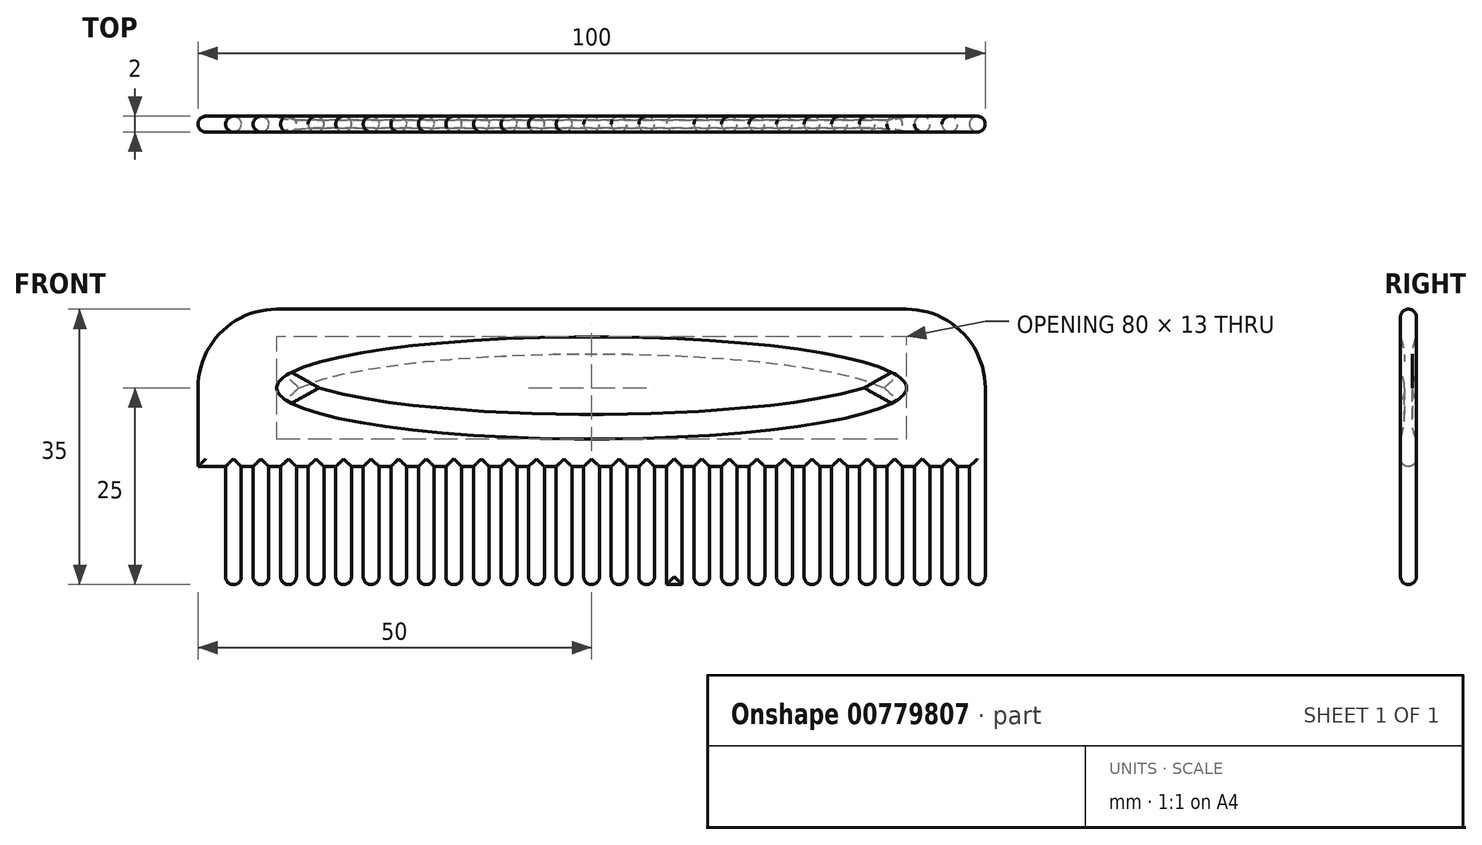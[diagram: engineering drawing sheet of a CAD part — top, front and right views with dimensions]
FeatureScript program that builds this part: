
annotation { "Feature Type Name" : "Feature", "Feature Type Description" : "" }
export const myFeature = defineFeature(function(context is Context, id is Id, definition is map)
    precondition{}
    {
        {
            var Q0;
            Q0=qCreatedBy(makeId("Front.planeOp"),FACE);
            var sketch = newSketch(context, id + "F0", { "sketchPlane" : qUnion([Q0])});
            skLineSegment(sketch, "E0.bottom", {"start": v(40, 10) * mm, "end": v(-40, 10) * mm});
            skLineSegment(sketch, "E0.top", {"start": v(50, -10) * mm, "end": v(-50, -10) * mm});
            skLineSegment(sketch, "E0.left", {"start": v(50, 0) * mm, "end": v(50, -10) * mm});
            skLineSegment(sketch, "E0.right", {"start": v(-50, 0) * mm, "end": v(-50, -10) * mm});
            skPoint(sketch, "E0.middle", {"position": v(0, 0) * mm});
            skPoint(sketch, "E1.visualSharp", {"position": v(-50, 10) * mm});
            skArc(sketch, "E1.filletArc", {"start": v(-40, 10) * mm, "mid": v(-47.07, 7.07) * mm, "end": v(-50, 0) * mm});
            skPoint(sketch, "E2.visualSharp", {"position": v(50, 10) * mm});
            skArc(sketch, "E2.filletArc", {"start": v(50, 0) * mm, "mid": v(47.07, 7.07) * mm, "end": v(40, 10) * mm});
            skLineSegment(sketch, "E3.bottom", {"start": v(-50, -10) * mm, "end": v(-48, -10) * mm});
            skLineSegment(sketch, "E3.top", {"start": v(-50, -25) * mm, "end": v(-48, -25) * mm});
            skLineSegment(sketch, "E3.left", {"start": v(-50, -10) * mm, "end": v(-50, -25) * mm});
            skLineSegment(sketch, "E3.right", {"start": v(-48, -10) * mm, "end": v(-48, -25) * mm});
            skLineSegment(sketch, "E4.1.0.0", {"start": v(-46.5, -10) * mm, "end": v(-46.5, -25) * mm});
            skLineSegment(sketch, "E4.1.0.1", {"start": v(-44.5, -10) * mm, "end": v(-44.5, -25) * mm});
            skLineSegment(sketch, "E4.1.0.2", {"start": v(-46.5, -25) * mm, "end": v(-44.5, -25) * mm});
            skLineSegment(sketch, "E4.2.0.0", {"start": v(-43, -10) * mm, "end": v(-43, -25) * mm});
            skLineSegment(sketch, "E4.2.0.1", {"start": v(-41, -10) * mm, "end": v(-41, -25) * mm});
            skLineSegment(sketch, "E4.2.0.2", {"start": v(-43, -25) * mm, "end": v(-41, -25) * mm});
            skLineSegment(sketch, "E4.3.0.0", {"start": v(-39.5, -10) * mm, "end": v(-39.5, -25) * mm});
            skLineSegment(sketch, "E4.3.0.1", {"start": v(-37.5, -10) * mm, "end": v(-37.5, -25) * mm});
            skLineSegment(sketch, "E4.3.0.2", {"start": v(-39.5, -25) * mm, "end": v(-37.5, -25) * mm});
            skLineSegment(sketch, "E4.4.0.0", {"start": v(-36, -10) * mm, "end": v(-36, -25) * mm});
            skLineSegment(sketch, "E4.4.0.1", {"start": v(-34, -10) * mm, "end": v(-34, -25) * mm});
            skLineSegment(sketch, "E4.4.0.2", {"start": v(-36, -25) * mm, "end": v(-34, -25) * mm});
            skLineSegment(sketch, "E4.5.0.0", {"start": v(-32.5, -10) * mm, "end": v(-32.5, -25) * mm});
            skLineSegment(sketch, "E4.5.0.1", {"start": v(-30.5, -10) * mm, "end": v(-30.5, -25) * mm});
            skLineSegment(sketch, "E4.5.0.2", {"start": v(-32.5, -25) * mm, "end": v(-30.5, -25) * mm});
            skLineSegment(sketch, "E4.6.0.0", {"start": v(-29, -10) * mm, "end": v(-29, -25) * mm});
            skLineSegment(sketch, "E4.6.0.1", {"start": v(-27, -10) * mm, "end": v(-27, -25) * mm});
            skLineSegment(sketch, "E4.6.0.2", {"start": v(-29, -25) * mm, "end": v(-27, -25) * mm});
            skLineSegment(sketch, "E4.7.0.0", {"start": v(-25.5, -10) * mm, "end": v(-25.5, -25) * mm});
            skLineSegment(sketch, "E4.7.0.1", {"start": v(-23.5, -10) * mm, "end": v(-23.5, -25) * mm});
            skLineSegment(sketch, "E4.7.0.2", {"start": v(-25.5, -25) * mm, "end": v(-23.5, -25) * mm});
            skLineSegment(sketch, "E4.8.0.0", {"start": v(-22, -10) * mm, "end": v(-22, -25) * mm});
            skLineSegment(sketch, "E4.8.0.1", {"start": v(-20, -10) * mm, "end": v(-20, -25) * mm});
            skLineSegment(sketch, "E4.8.0.2", {"start": v(-22, -25) * mm, "end": v(-20, -25) * mm});
            skLineSegment(sketch, "E4.9.0.0", {"start": v(-18.5, -10) * mm, "end": v(-18.5, -25) * mm});
            skLineSegment(sketch, "E4.9.0.1", {"start": v(-16.5, -10) * mm, "end": v(-16.5, -25) * mm});
            skLineSegment(sketch, "E4.9.0.2", {"start": v(-18.5, -25) * mm, "end": v(-16.5, -25) * mm});
            skLineSegment(sketch, "E4.10.0.0", {"start": v(-15, -10) * mm, "end": v(-15, -25) * mm});
            skLineSegment(sketch, "E4.10.0.1", {"start": v(-13, -10) * mm, "end": v(-13, -25) * mm});
            skLineSegment(sketch, "E4.10.0.2", {"start": v(-15, -25) * mm, "end": v(-13, -25) * mm});
            skLineSegment(sketch, "E4.11.0.0", {"start": v(-11.5, -10) * mm, "end": v(-11.5, -25) * mm});
            skLineSegment(sketch, "E4.11.0.1", {"start": v(-9.5, -10) * mm, "end": v(-9.5, -25) * mm});
            skLineSegment(sketch, "E4.11.0.2", {"start": v(-11.5, -25) * mm, "end": v(-9.5, -25) * mm});
            skLineSegment(sketch, "E4.12.0.0", {"start": v(-8, -10) * mm, "end": v(-8, -25) * mm});
            skLineSegment(sketch, "E4.12.0.1", {"start": v(-6, -10) * mm, "end": v(-6, -25) * mm});
            skLineSegment(sketch, "E4.12.0.2", {"start": v(-8, -25) * mm, "end": v(-6, -25) * mm});
            skLineSegment(sketch, "E4.13.0.0", {"start": v(-4.5, -10) * mm, "end": v(-4.5, -25) * mm});
            skLineSegment(sketch, "E4.13.0.1", {"start": v(-2.5, -10) * mm, "end": v(-2.5, -25) * mm});
            skLineSegment(sketch, "E4.13.0.2", {"start": v(-4.5, -25) * mm, "end": v(-2.5, -25) * mm});
            skLineSegment(sketch, "E4.14.0.0", {"start": v(-1, -10) * mm, "end": v(-1, -25) * mm});
            skLineSegment(sketch, "E4.14.0.1", {"start": v(1, -10) * mm, "end": v(1, -25) * mm});
            skLineSegment(sketch, "E4.14.0.2", {"start": v(-1, -25) * mm, "end": v(1, -25) * mm});
            skLineSegment(sketch, "E4.15.0.0", {"start": v(2.5, -10) * mm, "end": v(2.5, -25) * mm});
            skLineSegment(sketch, "E4.15.0.1", {"start": v(4.5, -10) * mm, "end": v(4.5, -25) * mm});
            skLineSegment(sketch, "E4.15.0.2", {"start": v(2.5, -25) * mm, "end": v(4.5, -25) * mm});
            skLineSegment(sketch, "E4.16.0.0", {"start": v(6, -10) * mm, "end": v(6, -25) * mm});
            skLineSegment(sketch, "E4.16.0.1", {"start": v(8, -10) * mm, "end": v(8, -25) * mm});
            skLineSegment(sketch, "E4.16.0.2", {"start": v(6, -25) * mm, "end": v(8, -25) * mm});
            skLineSegment(sketch, "E4.17.0.0", {"start": v(9.5, -10) * mm, "end": v(9.5, -25) * mm});
            skLineSegment(sketch, "E4.17.0.1", {"start": v(11.5, -10) * mm, "end": v(11.5, -25) * mm});
            skLineSegment(sketch, "E4.17.0.2", {"start": v(9.5, -25) * mm, "end": v(11.5, -25) * mm});
            skLineSegment(sketch, "E4.18.0.0", {"start": v(13, -10) * mm, "end": v(13, -25) * mm});
            skLineSegment(sketch, "E4.18.0.1", {"start": v(15, -10) * mm, "end": v(15, -25) * mm});
            skLineSegment(sketch, "E4.18.0.2", {"start": v(13, -25) * mm, "end": v(15, -25) * mm});
            skLineSegment(sketch, "E4.19.0.0", {"start": v(16.5, -10) * mm, "end": v(16.5, -25) * mm});
            skLineSegment(sketch, "E4.19.0.1", {"start": v(18.5, -10) * mm, "end": v(18.5, -25) * mm});
            skLineSegment(sketch, "E4.19.0.2", {"start": v(16.5, -25) * mm, "end": v(18.5, -25) * mm});
            skLineSegment(sketch, "E4.20.0.0", {"start": v(20, -10) * mm, "end": v(20, -25) * mm});
            skLineSegment(sketch, "E4.20.0.1", {"start": v(22, -10) * mm, "end": v(22, -25) * mm});
            skLineSegment(sketch, "E4.20.0.2", {"start": v(20, -25) * mm, "end": v(22, -25) * mm});
            skLineSegment(sketch, "E4.21.0.0", {"start": v(23.5, -10) * mm, "end": v(23.5, -25) * mm});
            skLineSegment(sketch, "E4.21.0.1", {"start": v(25.5, -10) * mm, "end": v(25.5, -25) * mm});
            skLineSegment(sketch, "E4.21.0.2", {"start": v(23.5, -25) * mm, "end": v(25.5, -25) * mm});
            skLineSegment(sketch, "E4.22.0.0", {"start": v(27, -10) * mm, "end": v(27, -25) * mm});
            skLineSegment(sketch, "E4.22.0.1", {"start": v(29, -10) * mm, "end": v(29, -25) * mm});
            skLineSegment(sketch, "E4.22.0.2", {"start": v(27, -25) * mm, "end": v(29, -25) * mm});
            skLineSegment(sketch, "E4.23.0.0", {"start": v(30.5, -10) * mm, "end": v(30.5, -25) * mm});
            skLineSegment(sketch, "E4.23.0.1", {"start": v(32.5, -10) * mm, "end": v(32.5, -25) * mm});
            skLineSegment(sketch, "E4.23.0.2", {"start": v(30.5, -25) * mm, "end": v(32.5, -25) * mm});
            skLineSegment(sketch, "E4.24.0.0", {"start": v(34, -10) * mm, "end": v(34, -25) * mm});
            skLineSegment(sketch, "E4.24.0.1", {"start": v(36, -10) * mm, "end": v(36, -25) * mm});
            skLineSegment(sketch, "E4.24.0.2", {"start": v(34, -25) * mm, "end": v(36, -25) * mm});
            skLineSegment(sketch, "E4.25.0.0", {"start": v(37.5, -10) * mm, "end": v(37.5, -25) * mm});
            skLineSegment(sketch, "E4.25.0.1", {"start": v(39.5, -10) * mm, "end": v(39.5, -25) * mm});
            skLineSegment(sketch, "E4.25.0.2", {"start": v(37.5, -25) * mm, "end": v(39.5, -25) * mm});
            skLineSegment(sketch, "E4.26.0.0", {"start": v(41, -10) * mm, "end": v(41, -25) * mm});
            skLineSegment(sketch, "E4.26.0.1", {"start": v(43, -10) * mm, "end": v(43, -25) * mm});
            skLineSegment(sketch, "E4.26.0.2", {"start": v(41, -25) * mm, "end": v(43, -25) * mm});
            skLineSegment(sketch, "E4.direction1", {"start": v(-50, -25) * mm, "end": v(-46.5, -25) * mm, "construction": true});
            skLineSegment(sketch, "E5.0.27.0", {"start": v(44.5, -10) * mm, "end": v(44.5, -25) * mm});
            skLineSegment(sketch, "E5.3.27.0", {"start": v(46.5, -10) * mm, "end": v(46.5, -25) * mm});
            skLineSegment(sketch, "E5.6.27.0", {"start": v(44.5, -25) * mm, "end": v(46.5, -25) * mm});
            skLineSegment(sketch, "E6.0.28.0", {"start": v(48, -10) * mm, "end": v(48, -25) * mm});
            skLineSegment(sketch, "E6.3.28.0", {"start": v(50, -10) * mm, "end": v(50, -25) * mm});
            skLineSegment(sketch, "E6.6.28.0", {"start": v(48, -25) * mm, "end": v(50, -25) * mm});
            skSolve(sketch);
        }
        {
            var Q0;
            {var subQ0=sQuery(id+"F0.wireOp",EDGE,"E4.1.0.0");Q0=makeQuery(id+"F0.imprint","IMPRINT",FACE,{"disambiguationData":[TD([[makeQuery(id+"F0.imprint","IMPRINT",EDGE,{"derivedFrom":subQ0}),1.0]])]});}
            var Q1;
            Q1=makeQuery(id+"F0.imprint","IMPRINT",FACE,{"disambiguationData":[TD([[makeQuery(id+"F0.imprint","IMPRINT",EDGE,{"derivedFrom":sQuery(id+"F0.wireOp",EDGE,"E3.bottom")}),-1.0]])]});
            var Q2;
            {var subQ0=sQuery(id+"F0.wireOp",EDGE,"E4.6.0.0");Q2=makeQuery(id+"F0.imprint","IMPRINT",FACE,{"disambiguationData":[TD([[makeQuery(id+"F0.imprint","IMPRINT",EDGE,{"derivedFrom":subQ0}),1.0]])]});}
            var Q3;
            {var subQ0=sQuery(id+"F0.wireOp",EDGE,"E4.13.0.0");Q3=makeQuery(id+"F0.imprint","IMPRINT",FACE,{"disambiguationData":[TD([[makeQuery(id+"F0.imprint","IMPRINT",EDGE,{"derivedFrom":subQ0}),1.0]])]});}
            var Q4;
            {var subQ0=sQuery(id+"F0.wireOp",EDGE,"E4.17.0.0");Q4=makeQuery(id+"F0.imprint","IMPRINT",FACE,{"disambiguationData":[TD([[makeQuery(id+"F0.imprint","IMPRINT",EDGE,{"derivedFrom":subQ0}),1.0]])]});}
            var Q5;
            {var subQ0=sQuery(id+"F0.wireOp",EDGE,"E4.16.0.0");Q5=makeQuery(id+"F0.imprint","IMPRINT",FACE,{"disambiguationData":[TD([[makeQuery(id+"F0.imprint","IMPRINT",EDGE,{"derivedFrom":subQ0}),1.0]])]});}
            var Q6;
            {var subQ0=sQuery(id+"F0.wireOp",EDGE,"E4.20.0.0");Q6=makeQuery(id+"F0.imprint","IMPRINT",FACE,{"disambiguationData":[TD([[makeQuery(id+"F0.imprint","IMPRINT",EDGE,{"derivedFrom":subQ0}),1.0]])]});}
            var Q7;
            {var subQ0=sQuery(id+"F0.wireOp",EDGE,"E4.5.0.0");Q7=makeQuery(id+"F0.imprint","IMPRINT",FACE,{"disambiguationData":[TD([[makeQuery(id+"F0.imprint","IMPRINT",EDGE,{"derivedFrom":subQ0}),1.0]])]});}
            var Q8;
            {var subQ0=sQuery(id+"F0.wireOp",EDGE,"E4.19.0.0");Q8=makeQuery(id+"F0.imprint","IMPRINT",FACE,{"disambiguationData":[TD([[makeQuery(id+"F0.imprint","IMPRINT",EDGE,{"derivedFrom":subQ0}),1.0]])]});}
            var Q9;
            Q9=makeQuery(id+"F0.imprint","IMPRINT",FACE,{"disambiguationData":[TD([[makeQuery(id+"F0.imprint","IMPRINT",EDGE,{"derivedFrom":sQuery(id+"F0.wireOp",EDGE,"E0.bottom")}),1.0]])]});
            var Q10;
            {var subQ0=sQuery(id+"F0.wireOp",EDGE,"E4.7.0.0");Q10=makeQuery(id+"F0.imprint","IMPRINT",FACE,{"disambiguationData":[TD([[makeQuery(id+"F0.imprint","IMPRINT",EDGE,{"derivedFrom":subQ0}),1.0]])]});}
            var Q11;
            {var subQ0=sQuery(id+"F0.wireOp",EDGE,"E4.8.0.0");Q11=makeQuery(id+"F0.imprint","IMPRINT",FACE,{"disambiguationData":[TD([[makeQuery(id+"F0.imprint","IMPRINT",EDGE,{"derivedFrom":subQ0}),1.0]])]});}
            var Q12;
            {var subQ0=sQuery(id+"F0.wireOp",EDGE,"E4.21.0.0");Q12=makeQuery(id+"F0.imprint","IMPRINT",FACE,{"disambiguationData":[TD([[makeQuery(id+"F0.imprint","IMPRINT",EDGE,{"derivedFrom":subQ0}),1.0]])]});}
            var Q13;
            {var subQ0=sQuery(id+"F0.wireOp",EDGE,"E4.18.0.0");Q13=makeQuery(id+"F0.imprint","IMPRINT",FACE,{"disambiguationData":[TD([[makeQuery(id+"F0.imprint","IMPRINT",EDGE,{"derivedFrom":subQ0}),1.0]])]});}
            var Q14;
            {var subQ0=sQuery(id+"F0.wireOp",EDGE,"E4.15.0.0");Q14=makeQuery(id+"F0.imprint","IMPRINT",FACE,{"disambiguationData":[TD([[makeQuery(id+"F0.imprint","IMPRINT",EDGE,{"derivedFrom":subQ0}),1.0]])]});}
            var Q15;
            {var subQ0=sQuery(id+"F0.wireOp",EDGE,"E4.14.0.0");Q15=makeQuery(id+"F0.imprint","IMPRINT",FACE,{"disambiguationData":[TD([[makeQuery(id+"F0.imprint","IMPRINT",EDGE,{"derivedFrom":subQ0}),1.0]])]});}
            var Q16;
            {var subQ0=sQuery(id+"F0.wireOp",EDGE,"E4.12.0.0");Q16=makeQuery(id+"F0.imprint","IMPRINT",FACE,{"disambiguationData":[TD([[makeQuery(id+"F0.imprint","IMPRINT",EDGE,{"derivedFrom":subQ0}),1.0]])]});}
            var Q17;
            {var subQ2=sQuery(id+"F0.wireOp",EDGE,"E6.0.28.0");Q17=makeQuery(id+"F0.imprint","IMPRINT",FACE,{"disambiguationData":[TD([[makeQuery(id+"F0.imprint","IMPRINT",EDGE,{"derivedFrom":subQ2}),1.0]])]});}
            var Q18;
            {var subQ0=sQuery(id+"F0.wireOp",EDGE,"E5.0.27.0");Q18=makeQuery(id+"F0.imprint","IMPRINT",FACE,{"disambiguationData":[TD([[makeQuery(id+"F0.imprint","IMPRINT",EDGE,{"derivedFrom":subQ0}),1.0]])]});}
            var Q19;
            {var subQ0=sQuery(id+"F0.wireOp",EDGE,"E4.26.0.0");Q19=makeQuery(id+"F0.imprint","IMPRINT",FACE,{"disambiguationData":[TD([[makeQuery(id+"F0.imprint","IMPRINT",EDGE,{"derivedFrom":subQ0}),1.0]])]});}
            var Q20;
            {var subQ0=sQuery(id+"F0.wireOp",EDGE,"E4.25.0.0");Q20=makeQuery(id+"F0.imprint","IMPRINT",FACE,{"disambiguationData":[TD([[makeQuery(id+"F0.imprint","IMPRINT",EDGE,{"derivedFrom":subQ0}),1.0]])]});}
            var Q21;
            {var subQ0=sQuery(id+"F0.wireOp",EDGE,"E4.24.0.0");Q21=makeQuery(id+"F0.imprint","IMPRINT",FACE,{"disambiguationData":[TD([[makeQuery(id+"F0.imprint","IMPRINT",EDGE,{"derivedFrom":subQ0}),1.0]])]});}
            var Q22;
            {var subQ0=sQuery(id+"F0.wireOp",EDGE,"E4.23.0.0");Q22=makeQuery(id+"F0.imprint","IMPRINT",FACE,{"disambiguationData":[TD([[makeQuery(id+"F0.imprint","IMPRINT",EDGE,{"derivedFrom":subQ0}),1.0]])]});}
            var Q23;
            {var subQ0=sQuery(id+"F0.wireOp",EDGE,"E4.22.0.0");Q23=makeQuery(id+"F0.imprint","IMPRINT",FACE,{"disambiguationData":[TD([[makeQuery(id+"F0.imprint","IMPRINT",EDGE,{"derivedFrom":subQ0}),1.0]])]});}
            var Q24;
            {var subQ0=sQuery(id+"F0.wireOp",EDGE,"E4.9.0.0");Q24=makeQuery(id+"F0.imprint","IMPRINT",FACE,{"disambiguationData":[TD([[makeQuery(id+"F0.imprint","IMPRINT",EDGE,{"derivedFrom":subQ0}),1.0]])]});}
            var Q25;
            {var subQ0=sQuery(id+"F0.wireOp",EDGE,"E4.2.0.0");Q25=makeQuery(id+"F0.imprint","IMPRINT",FACE,{"disambiguationData":[TD([[makeQuery(id+"F0.imprint","IMPRINT",EDGE,{"derivedFrom":subQ0}),1.0]])]});}
            var Q26;
            {var subQ0=sQuery(id+"F0.wireOp",EDGE,"E4.11.0.0");Q26=makeQuery(id+"F0.imprint","IMPRINT",FACE,{"disambiguationData":[TD([[makeQuery(id+"F0.imprint","IMPRINT",EDGE,{"derivedFrom":subQ0}),1.0]])]});}
            var Q27;
            {var subQ0=sQuery(id+"F0.wireOp",EDGE,"E4.10.0.0");Q27=makeQuery(id+"F0.imprint","IMPRINT",FACE,{"disambiguationData":[TD([[makeQuery(id+"F0.imprint","IMPRINT",EDGE,{"derivedFrom":subQ0}),1.0]])]});}
            var Q28;
            {var subQ0=sQuery(id+"F0.wireOp",EDGE,"E4.4.0.0");Q28=makeQuery(id+"F0.imprint","IMPRINT",FACE,{"disambiguationData":[TD([[makeQuery(id+"F0.imprint","IMPRINT",EDGE,{"derivedFrom":subQ0}),1.0]])]});}
            var Q29;
            {var subQ0=sQuery(id+"F0.wireOp",EDGE,"E4.3.0.0");Q29=makeQuery(id+"F0.imprint","IMPRINT",FACE,{"disambiguationData":[TD([[makeQuery(id+"F0.imprint","IMPRINT",EDGE,{"derivedFrom":subQ0}),1.0]])]});}
            extrude(context, id + "F1", {"entities" : qUnion([Q0, Q1, Q2, Q3, Q4, Q5, Q6, Q7, Q8, Q9, Q10, Q11, Q12, Q13, Q14, Q15, Q16, Q17, Q18, Q19, Q20, Q21, Q22, Q23, Q24, Q25, Q26, Q27, Q28, Q29]), "depth" : 2 * mm, "offsetDistance" : 25 * mm});
        }
        {
            var Q0;
            Q0=makeQuery(id+"F1.opExtrude","CAP_FACE",FACE,{"disambiguationData":[OSD([sQuery(id+"F0.wireOp",EDGE,"E0.bottom"),sQuery(id+"F0.wireOp",EDGE,"E0.top"),sQuery(id+"F0.wireOp",EDGE,"E0.left"),sQuery(id+"F0.wireOp",EDGE,"E0.right"),sQuery(id+"F0.wireOp",EDGE,"E1.filletArc"),sQuery(id+"F0.wireOp",EDGE,"E2.filletArc"),sQuery(id+"F0.wireOp",EDGE,"E3.top"),sQuery(id+"F0.wireOp",EDGE,"E3.left"),sQuery(id+"F0.wireOp",EDGE,"E3.right"),sQuery(id+"F0.wireOp",EDGE,"E4.1.0.0"),sQuery(id+"F0.wireOp",EDGE,"E4.1.0.1"),sQuery(id+"F0.wireOp",EDGE,"E4.1.0.2"),sQuery(id+"F0.wireOp",EDGE,"E4.2.0.0"),sQuery(id+"F0.wireOp",EDGE,"E4.2.0.1"),sQuery(id+"F0.wireOp",EDGE,"E4.2.0.2"),sQuery(id+"F0.wireOp",EDGE,"E4.3.0.0"),sQuery(id+"F0.wireOp",EDGE,"E4.3.0.1"),sQuery(id+"F0.wireOp",EDGE,"E4.3.0.2"),sQuery(id+"F0.wireOp",EDGE,"E4.4.0.0"),sQuery(id+"F0.wireOp",EDGE,"E4.4.0.1"),sQuery(id+"F0.wireOp",EDGE,"E4.4.0.2"),sQuery(id+"F0.wireOp",EDGE,"E4.5.0.0"),sQuery(id+"F0.wireOp",EDGE,"E4.5.0.1"),sQuery(id+"F0.wireOp",EDGE,"E4.5.0.2"),sQuery(id+"F0.wireOp",EDGE,"E4.6.0.0"),sQuery(id+"F0.wireOp",EDGE,"E4.6.0.1"),sQuery(id+"F0.wireOp",EDGE,"E4.6.0.2"),sQuery(id+"F0.wireOp",EDGE,"E4.7.0.0"),sQuery(id+"F0.wireOp",EDGE,"E4.7.0.1"),sQuery(id+"F0.wireOp",EDGE,"E4.7.0.2"),sQuery(id+"F0.wireOp",EDGE,"E4.8.0.0"),sQuery(id+"F0.wireOp",EDGE,"E4.8.0.1"),sQuery(id+"F0.wireOp",EDGE,"E4.8.0.2"),sQuery(id+"F0.wireOp",EDGE,"E4.9.0.0"),sQuery(id+"F0.wireOp",EDGE,"E4.9.0.1"),sQuery(id+"F0.wireOp",EDGE,"E4.9.0.2"),sQuery(id+"F0.wireOp",EDGE,"E4.10.0.0"),sQuery(id+"F0.wireOp",EDGE,"E4.10.0.1"),sQuery(id+"F0.wireOp",EDGE,"E4.10.0.2"),sQuery(id+"F0.wireOp",EDGE,"E4.11.0.0"),sQuery(id+"F0.wireOp",EDGE,"E4.11.0.1"),sQuery(id+"F0.wireOp",EDGE,"E4.11.0.2"),sQuery(id+"F0.wireOp",EDGE,"E4.12.0.0"),sQuery(id+"F0.wireOp",EDGE,"E4.12.0.1"),sQuery(id+"F0.wireOp",EDGE,"E4.12.0.2"),sQuery(id+"F0.wireOp",EDGE,"E4.13.0.0"),sQuery(id+"F0.wireOp",EDGE,"E4.13.0.1"),sQuery(id+"F0.wireOp",EDGE,"E4.13.0.2"),sQuery(id+"F0.wireOp",EDGE,"E4.14.0.0"),sQuery(id+"F0.wireOp",EDGE,"E4.14.0.1"),sQuery(id+"F0.wireOp",EDGE,"E4.14.0.2"),sQuery(id+"F0.wireOp",EDGE,"E4.15.0.0"),sQuery(id+"F0.wireOp",EDGE,"E4.15.0.1"),sQuery(id+"F0.wireOp",EDGE,"E4.15.0.2"),sQuery(id+"F0.wireOp",EDGE,"E4.16.0.0"),sQuery(id+"F0.wireOp",EDGE,"E4.16.0.1"),sQuery(id+"F0.wireOp",EDGE,"E4.16.0.2"),sQuery(id+"F0.wireOp",EDGE,"E4.17.0.0"),sQuery(id+"F0.wireOp",EDGE,"E4.17.0.1"),sQuery(id+"F0.wireOp",EDGE,"E4.17.0.2"),sQuery(id+"F0.wireOp",EDGE,"E4.18.0.0"),sQuery(id+"F0.wireOp",EDGE,"E4.18.0.1"),sQuery(id+"F0.wireOp",EDGE,"E4.18.0.2"),sQuery(id+"F0.wireOp",EDGE,"E4.19.0.0"),sQuery(id+"F0.wireOp",EDGE,"E4.19.0.1"),sQuery(id+"F0.wireOp",EDGE,"E4.19.0.2"),sQuery(id+"F0.wireOp",EDGE,"E4.20.0.0"),sQuery(id+"F0.wireOp",EDGE,"E4.20.0.1"),sQuery(id+"F0.wireOp",EDGE,"E4.20.0.2"),sQuery(id+"F0.wireOp",EDGE,"E4.21.0.0"),sQuery(id+"F0.wireOp",EDGE,"E4.21.0.1"),sQuery(id+"F0.wireOp",EDGE,"E4.21.0.2"),sQuery(id+"F0.wireOp",EDGE,"E4.22.0.0"),sQuery(id+"F0.wireOp",EDGE,"E4.22.0.1"),sQuery(id+"F0.wireOp",EDGE,"E4.22.0.2"),sQuery(id+"F0.wireOp",EDGE,"E4.23.0.0"),sQuery(id+"F0.wireOp",EDGE,"E4.23.0.1"),sQuery(id+"F0.wireOp",EDGE,"E4.23.0.2"),sQuery(id+"F0.wireOp",EDGE,"E4.24.0.0"),sQuery(id+"F0.wireOp",EDGE,"E4.24.0.1"),sQuery(id+"F0.wireOp",EDGE,"E4.24.0.2"),sQuery(id+"F0.wireOp",EDGE,"E4.25.0.0"),sQuery(id+"F0.wireOp",EDGE,"E4.25.0.1"),sQuery(id+"F0.wireOp",EDGE,"E4.25.0.2"),sQuery(id+"F0.wireOp",EDGE,"E4.26.0.0"),sQuery(id+"F0.wireOp",EDGE,"E4.26.0.1"),sQuery(id+"F0.wireOp",EDGE,"E4.26.0.2"),sQuery(id+"F0.wireOp",EDGE,"E5.0.27.0"),sQuery(id+"F0.wireOp",EDGE,"E5.3.27.0"),sQuery(id+"F0.wireOp",EDGE,"E5.6.27.0"),sQuery(id+"F0.wireOp",EDGE,"E6.0.28.0"),sQuery(id+"F0.wireOp",EDGE,"E6.3.28.0"),sQuery(id+"F0.wireOp",EDGE,"E6.6.28.0")])],"isStart":false});
            var Q1;
            Q1=makeQuery(id+"F1.opExtrude","CAP_FACE",FACE,{"disambiguationData":[OSD([sQuery(id+"F0.wireOp",EDGE,"E0.bottom"),sQuery(id+"F0.wireOp",EDGE,"E0.top"),sQuery(id+"F0.wireOp",EDGE,"E0.left"),sQuery(id+"F0.wireOp",EDGE,"E0.right"),sQuery(id+"F0.wireOp",EDGE,"E1.filletArc"),sQuery(id+"F0.wireOp",EDGE,"E2.filletArc"),sQuery(id+"F0.wireOp",EDGE,"E3.top"),sQuery(id+"F0.wireOp",EDGE,"E3.left"),sQuery(id+"F0.wireOp",EDGE,"E3.right"),sQuery(id+"F0.wireOp",EDGE,"E4.1.0.0"),sQuery(id+"F0.wireOp",EDGE,"E4.1.0.1"),sQuery(id+"F0.wireOp",EDGE,"E4.1.0.2"),sQuery(id+"F0.wireOp",EDGE,"E4.2.0.0"),sQuery(id+"F0.wireOp",EDGE,"E4.2.0.1"),sQuery(id+"F0.wireOp",EDGE,"E4.2.0.2"),sQuery(id+"F0.wireOp",EDGE,"E4.3.0.0"),sQuery(id+"F0.wireOp",EDGE,"E4.3.0.1"),sQuery(id+"F0.wireOp",EDGE,"E4.3.0.2"),sQuery(id+"F0.wireOp",EDGE,"E4.4.0.0"),sQuery(id+"F0.wireOp",EDGE,"E4.4.0.1"),sQuery(id+"F0.wireOp",EDGE,"E4.4.0.2"),sQuery(id+"F0.wireOp",EDGE,"E4.5.0.0"),sQuery(id+"F0.wireOp",EDGE,"E4.5.0.1"),sQuery(id+"F0.wireOp",EDGE,"E4.5.0.2"),sQuery(id+"F0.wireOp",EDGE,"E4.6.0.0"),sQuery(id+"F0.wireOp",EDGE,"E4.6.0.1"),sQuery(id+"F0.wireOp",EDGE,"E4.6.0.2"),sQuery(id+"F0.wireOp",EDGE,"E4.7.0.0"),sQuery(id+"F0.wireOp",EDGE,"E4.7.0.1"),sQuery(id+"F0.wireOp",EDGE,"E4.7.0.2"),sQuery(id+"F0.wireOp",EDGE,"E4.8.0.0"),sQuery(id+"F0.wireOp",EDGE,"E4.8.0.1"),sQuery(id+"F0.wireOp",EDGE,"E4.8.0.2"),sQuery(id+"F0.wireOp",EDGE,"E4.9.0.0"),sQuery(id+"F0.wireOp",EDGE,"E4.9.0.1"),sQuery(id+"F0.wireOp",EDGE,"E4.9.0.2"),sQuery(id+"F0.wireOp",EDGE,"E4.10.0.0"),sQuery(id+"F0.wireOp",EDGE,"E4.10.0.1"),sQuery(id+"F0.wireOp",EDGE,"E4.10.0.2"),sQuery(id+"F0.wireOp",EDGE,"E4.11.0.0"),sQuery(id+"F0.wireOp",EDGE,"E4.11.0.1"),sQuery(id+"F0.wireOp",EDGE,"E4.11.0.2"),sQuery(id+"F0.wireOp",EDGE,"E4.12.0.0"),sQuery(id+"F0.wireOp",EDGE,"E4.12.0.1"),sQuery(id+"F0.wireOp",EDGE,"E4.12.0.2"),sQuery(id+"F0.wireOp",EDGE,"E4.13.0.0"),sQuery(id+"F0.wireOp",EDGE,"E4.13.0.1"),sQuery(id+"F0.wireOp",EDGE,"E4.13.0.2"),sQuery(id+"F0.wireOp",EDGE,"E4.14.0.0"),sQuery(id+"F0.wireOp",EDGE,"E4.14.0.1"),sQuery(id+"F0.wireOp",EDGE,"E4.14.0.2"),sQuery(id+"F0.wireOp",EDGE,"E4.15.0.0"),sQuery(id+"F0.wireOp",EDGE,"E4.15.0.1"),sQuery(id+"F0.wireOp",EDGE,"E4.15.0.2"),sQuery(id+"F0.wireOp",EDGE,"E4.16.0.0"),sQuery(id+"F0.wireOp",EDGE,"E4.16.0.1"),sQuery(id+"F0.wireOp",EDGE,"E4.16.0.2"),sQuery(id+"F0.wireOp",EDGE,"E4.17.0.0"),sQuery(id+"F0.wireOp",EDGE,"E4.17.0.1"),sQuery(id+"F0.wireOp",EDGE,"E4.17.0.2"),sQuery(id+"F0.wireOp",EDGE,"E4.18.0.0"),sQuery(id+"F0.wireOp",EDGE,"E4.18.0.1"),sQuery(id+"F0.wireOp",EDGE,"E4.18.0.2"),sQuery(id+"F0.wireOp",EDGE,"E4.19.0.0"),sQuery(id+"F0.wireOp",EDGE,"E4.19.0.1"),sQuery(id+"F0.wireOp",EDGE,"E4.19.0.2"),sQuery(id+"F0.wireOp",EDGE,"E4.20.0.0"),sQuery(id+"F0.wireOp",EDGE,"E4.20.0.1"),sQuery(id+"F0.wireOp",EDGE,"E4.20.0.2"),sQuery(id+"F0.wireOp",EDGE,"E4.21.0.0"),sQuery(id+"F0.wireOp",EDGE,"E4.21.0.1"),sQuery(id+"F0.wireOp",EDGE,"E4.21.0.2"),sQuery(id+"F0.wireOp",EDGE,"E4.22.0.0"),sQuery(id+"F0.wireOp",EDGE,"E4.22.0.1"),sQuery(id+"F0.wireOp",EDGE,"E4.22.0.2"),sQuery(id+"F0.wireOp",EDGE,"E4.23.0.0"),sQuery(id+"F0.wireOp",EDGE,"E4.23.0.1"),sQuery(id+"F0.wireOp",EDGE,"E4.23.0.2"),sQuery(id+"F0.wireOp",EDGE,"E4.24.0.0"),sQuery(id+"F0.wireOp",EDGE,"E4.24.0.1"),sQuery(id+"F0.wireOp",EDGE,"E4.24.0.2"),sQuery(id+"F0.wireOp",EDGE,"E4.25.0.0"),sQuery(id+"F0.wireOp",EDGE,"E4.25.0.1"),sQuery(id+"F0.wireOp",EDGE,"E4.25.0.2"),sQuery(id+"F0.wireOp",EDGE,"E4.26.0.0"),sQuery(id+"F0.wireOp",EDGE,"E4.26.0.1"),sQuery(id+"F0.wireOp",EDGE,"E4.26.0.2"),sQuery(id+"F0.wireOp",EDGE,"E5.0.27.0"),sQuery(id+"F0.wireOp",EDGE,"E5.3.27.0"),sQuery(id+"F0.wireOp",EDGE,"E5.6.27.0"),sQuery(id+"F0.wireOp",EDGE,"E6.0.28.0"),sQuery(id+"F0.wireOp",EDGE,"E6.3.28.0"),sQuery(id+"F0.wireOp",EDGE,"E6.6.28.0")])],"isStart":true});
            var Q2;
            Q2=makeQuery(id+"F1.opExtrude","SWEPT_FACE",FACE,{"disambiguationData":[OSD([sQuery(id+"F0.wireOp",EDGE,"E3.top")])]});
            var Q3;
            Q3=makeQuery(id+"F1.opExtrude","SWEPT_FACE",FACE,{"disambiguationData":[OSD([sQuery(id+"F0.wireOp",EDGE,"E4.1.0.2")])]});
            var Q4;
            Q4=makeQuery(id+"F1.opExtrude","SWEPT_FACE",FACE,{"disambiguationData":[OSD([sQuery(id+"F0.wireOp",EDGE,"E4.2.0.2")])]});
            var Q5;
            Q5=makeQuery(id+"F1.opExtrude","SWEPT_FACE",FACE,{"disambiguationData":[OSD([sQuery(id+"F0.wireOp",EDGE,"E4.3.0.2")])]});
            var Q6;
            Q6=makeQuery(id+"F1.opExtrude","SWEPT_FACE",FACE,{"disambiguationData":[OSD([sQuery(id+"F0.wireOp",EDGE,"E4.4.0.2")])]});
            var Q7;
            Q7=makeQuery(id+"F1.opExtrude","SWEPT_FACE",FACE,{"disambiguationData":[OSD([sQuery(id+"F0.wireOp",EDGE,"E4.5.0.2")])]});
            var Q8;
            Q8=makeQuery(id+"F1.opExtrude","SWEPT_FACE",FACE,{"disambiguationData":[OSD([sQuery(id+"F0.wireOp",EDGE,"E4.6.0.2")])]});
            var Q9;
            Q9=makeQuery(id+"F1.opExtrude","SWEPT_FACE",FACE,{"disambiguationData":[OSD([sQuery(id+"F0.wireOp",EDGE,"E4.7.0.2")])]});
            var Q10;
            Q10=makeQuery(id+"F1.opExtrude","SWEPT_FACE",FACE,{"disambiguationData":[OSD([sQuery(id+"F0.wireOp",EDGE,"E4.8.0.2")])]});
            var Q11;
            Q11=makeQuery(id+"F1.opExtrude","SWEPT_FACE",FACE,{"disambiguationData":[OSD([sQuery(id+"F0.wireOp",EDGE,"E4.9.0.2")])]});
            var Q12;
            Q12=makeQuery(id+"F1.opExtrude","SWEPT_FACE",FACE,{"disambiguationData":[OSD([sQuery(id+"F0.wireOp",EDGE,"E4.10.0.2")])]});
            var Q13;
            Q13=makeQuery(id+"F1.opExtrude","SWEPT_FACE",FACE,{"disambiguationData":[OSD([sQuery(id+"F0.wireOp",EDGE,"E4.11.0.2")])]});
            var Q14;
            Q14=makeQuery(id+"F1.opExtrude","SWEPT_FACE",FACE,{"disambiguationData":[OSD([sQuery(id+"F0.wireOp",EDGE,"E4.12.0.2")])]});
            var Q15;
            Q15=makeQuery(id+"F1.opExtrude","SWEPT_FACE",FACE,{"disambiguationData":[OSD([sQuery(id+"F0.wireOp",EDGE,"E4.13.0.2")])]});
            var Q16;
            Q16=makeQuery(id+"F1.opExtrude","SWEPT_FACE",FACE,{"disambiguationData":[OSD([sQuery(id+"F0.wireOp",EDGE,"E4.14.0.2")])]});
            var Q17;
            Q17=makeQuery(id+"F1.opExtrude","SWEPT_FACE",FACE,{"disambiguationData":[OSD([sQuery(id+"F0.wireOp",EDGE,"E4.15.0.2")])]});
            var Q18;
            Q18=makeQuery(id+"F1.opExtrude","SWEPT_FACE",FACE,{"disambiguationData":[OSD([sQuery(id+"F0.wireOp",EDGE,"E4.16.0.2")])]});
            var Q19;
            Q19=makeQuery(id+"F1.opExtrude","SWEPT_FACE",FACE,{"disambiguationData":[OSD([sQuery(id+"F0.wireOp",EDGE,"E4.18.0.2")])]});
            var Q20;
            Q20=makeQuery(id+"F1.opExtrude","SWEPT_FACE",FACE,{"disambiguationData":[OSD([sQuery(id+"F0.wireOp",EDGE,"E4.19.0.2")])]});
            var Q21;
            Q21=makeQuery(id+"F1.opExtrude","SWEPT_FACE",FACE,{"disambiguationData":[OSD([sQuery(id+"F0.wireOp",EDGE,"E4.20.0.2")])]});
            var Q22;
            Q22=makeQuery(id+"F1.opExtrude","SWEPT_FACE",FACE,{"disambiguationData":[OSD([sQuery(id+"F0.wireOp",EDGE,"E4.21.0.2")])]});
            var Q23;
            Q23=makeQuery(id+"F1.opExtrude","SWEPT_FACE",FACE,{"disambiguationData":[OSD([sQuery(id+"F0.wireOp",EDGE,"E4.22.0.2")])]});
            var Q24;
            Q24=makeQuery(id+"F1.opExtrude","SWEPT_FACE",FACE,{"disambiguationData":[OSD([sQuery(id+"F0.wireOp",EDGE,"E4.23.0.2")])]});
            var Q25;
            Q25=makeQuery(id+"F1.opExtrude","SWEPT_FACE",FACE,{"disambiguationData":[OSD([sQuery(id+"F0.wireOp",EDGE,"E4.24.0.2")])]});
            var Q26;
            Q26=makeQuery(id+"F1.opExtrude","SWEPT_FACE",FACE,{"disambiguationData":[OSD([sQuery(id+"F0.wireOp",EDGE,"E4.25.0.2")])]});
            var Q27;
            Q27=makeQuery(id+"F1.opExtrude","SWEPT_FACE",FACE,{"disambiguationData":[OSD([sQuery(id+"F0.wireOp",EDGE,"E4.26.0.2")])]});
            var Q28;
            Q28=makeQuery(id+"F1.opExtrude","SWEPT_FACE",FACE,{"disambiguationData":[OSD([sQuery(id+"F0.wireOp",EDGE,"E5.6.27.0")])]});
            var Q29;
            Q29=makeQuery(id+"F1.opExtrude","SWEPT_FACE",FACE,{"disambiguationData":[OSD([sQuery(id+"F0.wireOp",EDGE,"E6.6.28.0")])]});
            fillet(context, id + "F2", {"entities" : qUnion([Q0, Q1, Q2, Q3, Q4, Q5, Q6, Q7, Q8, Q9, Q10, Q11, Q12, Q13, Q14, Q15, Q16, Q17, Q18, Q19, Q20, Q21, Q22, Q23, Q24, Q25, Q26, Q27, Q28, Q29]), "radius" : 1 * mm, "tangentPropagation" : true, "allowEdgeOverflow" : false});
        }
        {
            var Q0;
            Q0=makeQuery(id+"F1.opExtrude","CAP_FACE",FACE,{"disambiguationData":[OSD([sQuery(id+"F0.wireOp",EDGE,"E0.bottom"),sQuery(id+"F0.wireOp",EDGE,"E0.top"),sQuery(id+"F0.wireOp",EDGE,"E0.left"),sQuery(id+"F0.wireOp",EDGE,"E0.right"),sQuery(id+"F0.wireOp",EDGE,"E1.filletArc"),sQuery(id+"F0.wireOp",EDGE,"E2.filletArc"),sQuery(id+"F0.wireOp",EDGE,"E3.top"),sQuery(id+"F0.wireOp",EDGE,"E3.left"),sQuery(id+"F0.wireOp",EDGE,"E3.right"),sQuery(id+"F0.wireOp",EDGE,"E4.1.0.0"),sQuery(id+"F0.wireOp",EDGE,"E4.1.0.1"),sQuery(id+"F0.wireOp",EDGE,"E4.1.0.2"),sQuery(id+"F0.wireOp",EDGE,"E4.2.0.0"),sQuery(id+"F0.wireOp",EDGE,"E4.2.0.1"),sQuery(id+"F0.wireOp",EDGE,"E4.2.0.2"),sQuery(id+"F0.wireOp",EDGE,"E4.3.0.0"),sQuery(id+"F0.wireOp",EDGE,"E4.3.0.1"),sQuery(id+"F0.wireOp",EDGE,"E4.3.0.2"),sQuery(id+"F0.wireOp",EDGE,"E4.4.0.0"),sQuery(id+"F0.wireOp",EDGE,"E4.4.0.1"),sQuery(id+"F0.wireOp",EDGE,"E4.4.0.2"),sQuery(id+"F0.wireOp",EDGE,"E4.5.0.0"),sQuery(id+"F0.wireOp",EDGE,"E4.5.0.1"),sQuery(id+"F0.wireOp",EDGE,"E4.5.0.2"),sQuery(id+"F0.wireOp",EDGE,"E4.6.0.0"),sQuery(id+"F0.wireOp",EDGE,"E4.6.0.1"),sQuery(id+"F0.wireOp",EDGE,"E4.6.0.2"),sQuery(id+"F0.wireOp",EDGE,"E4.7.0.0"),sQuery(id+"F0.wireOp",EDGE,"E4.7.0.1"),sQuery(id+"F0.wireOp",EDGE,"E4.7.0.2"),sQuery(id+"F0.wireOp",EDGE,"E4.8.0.0"),sQuery(id+"F0.wireOp",EDGE,"E4.8.0.1"),sQuery(id+"F0.wireOp",EDGE,"E4.8.0.2"),sQuery(id+"F0.wireOp",EDGE,"E4.9.0.0"),sQuery(id+"F0.wireOp",EDGE,"E4.9.0.1"),sQuery(id+"F0.wireOp",EDGE,"E4.9.0.2"),sQuery(id+"F0.wireOp",EDGE,"E4.10.0.0"),sQuery(id+"F0.wireOp",EDGE,"E4.10.0.1"),sQuery(id+"F0.wireOp",EDGE,"E4.10.0.2"),sQuery(id+"F0.wireOp",EDGE,"E4.11.0.0"),sQuery(id+"F0.wireOp",EDGE,"E4.11.0.1"),sQuery(id+"F0.wireOp",EDGE,"E4.11.0.2"),sQuery(id+"F0.wireOp",EDGE,"E4.12.0.0"),sQuery(id+"F0.wireOp",EDGE,"E4.12.0.1"),sQuery(id+"F0.wireOp",EDGE,"E4.12.0.2"),sQuery(id+"F0.wireOp",EDGE,"E4.13.0.0"),sQuery(id+"F0.wireOp",EDGE,"E4.13.0.1"),sQuery(id+"F0.wireOp",EDGE,"E4.13.0.2"),sQuery(id+"F0.wireOp",EDGE,"E4.14.0.0"),sQuery(id+"F0.wireOp",EDGE,"E4.14.0.1"),sQuery(id+"F0.wireOp",EDGE,"E4.14.0.2"),sQuery(id+"F0.wireOp",EDGE,"E4.15.0.0"),sQuery(id+"F0.wireOp",EDGE,"E4.15.0.1"),sQuery(id+"F0.wireOp",EDGE,"E4.15.0.2"),sQuery(id+"F0.wireOp",EDGE,"E4.16.0.0"),sQuery(id+"F0.wireOp",EDGE,"E4.16.0.1"),sQuery(id+"F0.wireOp",EDGE,"E4.16.0.2"),sQuery(id+"F0.wireOp",EDGE,"E4.17.0.0"),sQuery(id+"F0.wireOp",EDGE,"E4.17.0.1"),sQuery(id+"F0.wireOp",EDGE,"E4.17.0.2"),sQuery(id+"F0.wireOp",EDGE,"E4.18.0.0"),sQuery(id+"F0.wireOp",EDGE,"E4.18.0.1"),sQuery(id+"F0.wireOp",EDGE,"E4.18.0.2"),sQuery(id+"F0.wireOp",EDGE,"E4.19.0.0"),sQuery(id+"F0.wireOp",EDGE,"E4.19.0.1"),sQuery(id+"F0.wireOp",EDGE,"E4.19.0.2"),sQuery(id+"F0.wireOp",EDGE,"E4.20.0.0"),sQuery(id+"F0.wireOp",EDGE,"E4.20.0.1"),sQuery(id+"F0.wireOp",EDGE,"E4.20.0.2"),sQuery(id+"F0.wireOp",EDGE,"E4.21.0.0"),sQuery(id+"F0.wireOp",EDGE,"E4.21.0.1"),sQuery(id+"F0.wireOp",EDGE,"E4.21.0.2"),sQuery(id+"F0.wireOp",EDGE,"E4.22.0.0"),sQuery(id+"F0.wireOp",EDGE,"E4.22.0.1"),sQuery(id+"F0.wireOp",EDGE,"E4.22.0.2"),sQuery(id+"F0.wireOp",EDGE,"E4.23.0.0"),sQuery(id+"F0.wireOp",EDGE,"E4.23.0.1"),sQuery(id+"F0.wireOp",EDGE,"E4.23.0.2"),sQuery(id+"F0.wireOp",EDGE,"E4.24.0.0"),sQuery(id+"F0.wireOp",EDGE,"E4.24.0.1"),sQuery(id+"F0.wireOp",EDGE,"E4.24.0.2"),sQuery(id+"F0.wireOp",EDGE,"E4.25.0.0"),sQuery(id+"F0.wireOp",EDGE,"E4.25.0.1"),sQuery(id+"F0.wireOp",EDGE,"E4.25.0.2"),sQuery(id+"F0.wireOp",EDGE,"E4.26.0.0"),sQuery(id+"F0.wireOp",EDGE,"E4.26.0.1"),sQuery(id+"F0.wireOp",EDGE,"E4.26.0.2"),sQuery(id+"F0.wireOp",EDGE,"E5.0.27.0"),sQuery(id+"F0.wireOp",EDGE,"E5.3.27.0"),sQuery(id+"F0.wireOp",EDGE,"E5.6.27.0"),sQuery(id+"F0.wireOp",EDGE,"E6.0.28.0"),sQuery(id+"F0.wireOp",EDGE,"E6.3.28.0"),sQuery(id+"F0.wireOp",EDGE,"E6.6.28.0")])],"isStart":false});
            var sketch = newSketch(context, id + "F3", { "sketchPlane" : qUnion([Q0])});
            skEllipse(sketch, "E7", {"center": v(0, 0) * mm, "majorRadius": 6.5 * mm, "minorRadius": 40 * mm, "majorAxis": v(0, 1)});
            skPoint(sketch, "E8", {"position": v(0, 6.5) * mm});
            skPoint(sketch, "E9", {"position": v(-40, 0) * mm});
            skPoint(sketch, "E10", {"position": v(0, -6.5) * mm});
            skPoint(sketch, "E11", {"position": v(40, 0) * mm});
            skSolve(sketch);
        }
        {
            var Q0;
            Q0=makeQuery(id+"F3.imprint","IMPRINT",FACE,{"disambiguationData":[TD([[makeQuery(id+"F3.imprint","IMPRINT",EDGE,{"derivedFrom":sQuery(id+"F3.wireOp",EDGE,"E7")}),1.0]])]});
            extrude(context, id + "F4", {"entities" : qUnion([Q0]), "operationType" : NewBodyOperationType.REMOVE, "oppositeDirection" : true, "depth" : 0.5 * mm, "offsetDistance" : 25 * mm});
        }
        {
            var Q0;
            Q0=makeQuery(id+"F4.boolean.opBoolean","COPY",FACE,{"derivedFrom":makeQuery(id+"F4.opExtrude","CAP_FACE",FACE,{"disambiguationData":[OSD([sQuery(id+"F3.wireOp",EDGE,"E7")])],"isStart":false})});
            fillet(context, id + "F5", {"entities" : qUnion([Q0]), "radius" : 10 * mm, "tangentPropagation" : true, "allowEdgeOverflow" : false});
        }
        {
            var Q0;
            Q0=makeQuery(id+"F1.opExtrude","CAP_FACE",FACE,{"disambiguationData":[OSD([sQuery(id+"F0.wireOp",EDGE,"E0.bottom"),sQuery(id+"F0.wireOp",EDGE,"E0.top"),sQuery(id+"F0.wireOp",EDGE,"E0.left"),sQuery(id+"F0.wireOp",EDGE,"E0.right"),sQuery(id+"F0.wireOp",EDGE,"E1.filletArc"),sQuery(id+"F0.wireOp",EDGE,"E2.filletArc"),sQuery(id+"F0.wireOp",EDGE,"E3.top"),sQuery(id+"F0.wireOp",EDGE,"E3.left"),sQuery(id+"F0.wireOp",EDGE,"E3.right"),sQuery(id+"F0.wireOp",EDGE,"E4.1.0.0"),sQuery(id+"F0.wireOp",EDGE,"E4.1.0.1"),sQuery(id+"F0.wireOp",EDGE,"E4.1.0.2"),sQuery(id+"F0.wireOp",EDGE,"E4.2.0.0"),sQuery(id+"F0.wireOp",EDGE,"E4.2.0.1"),sQuery(id+"F0.wireOp",EDGE,"E4.2.0.2"),sQuery(id+"F0.wireOp",EDGE,"E4.3.0.0"),sQuery(id+"F0.wireOp",EDGE,"E4.3.0.1"),sQuery(id+"F0.wireOp",EDGE,"E4.3.0.2"),sQuery(id+"F0.wireOp",EDGE,"E4.4.0.0"),sQuery(id+"F0.wireOp",EDGE,"E4.4.0.1"),sQuery(id+"F0.wireOp",EDGE,"E4.4.0.2"),sQuery(id+"F0.wireOp",EDGE,"E4.5.0.0"),sQuery(id+"F0.wireOp",EDGE,"E4.5.0.1"),sQuery(id+"F0.wireOp",EDGE,"E4.5.0.2"),sQuery(id+"F0.wireOp",EDGE,"E4.6.0.0"),sQuery(id+"F0.wireOp",EDGE,"E4.6.0.1"),sQuery(id+"F0.wireOp",EDGE,"E4.6.0.2"),sQuery(id+"F0.wireOp",EDGE,"E4.7.0.0"),sQuery(id+"F0.wireOp",EDGE,"E4.7.0.1"),sQuery(id+"F0.wireOp",EDGE,"E4.7.0.2"),sQuery(id+"F0.wireOp",EDGE,"E4.8.0.0"),sQuery(id+"F0.wireOp",EDGE,"E4.8.0.1"),sQuery(id+"F0.wireOp",EDGE,"E4.8.0.2"),sQuery(id+"F0.wireOp",EDGE,"E4.9.0.0"),sQuery(id+"F0.wireOp",EDGE,"E4.9.0.1"),sQuery(id+"F0.wireOp",EDGE,"E4.9.0.2"),sQuery(id+"F0.wireOp",EDGE,"E4.10.0.0"),sQuery(id+"F0.wireOp",EDGE,"E4.10.0.1"),sQuery(id+"F0.wireOp",EDGE,"E4.10.0.2"),sQuery(id+"F0.wireOp",EDGE,"E4.11.0.0"),sQuery(id+"F0.wireOp",EDGE,"E4.11.0.1"),sQuery(id+"F0.wireOp",EDGE,"E4.11.0.2"),sQuery(id+"F0.wireOp",EDGE,"E4.12.0.0"),sQuery(id+"F0.wireOp",EDGE,"E4.12.0.1"),sQuery(id+"F0.wireOp",EDGE,"E4.12.0.2"),sQuery(id+"F0.wireOp",EDGE,"E4.13.0.0"),sQuery(id+"F0.wireOp",EDGE,"E4.13.0.1"),sQuery(id+"F0.wireOp",EDGE,"E4.13.0.2"),sQuery(id+"F0.wireOp",EDGE,"E4.14.0.0"),sQuery(id+"F0.wireOp",EDGE,"E4.14.0.1"),sQuery(id+"F0.wireOp",EDGE,"E4.14.0.2"),sQuery(id+"F0.wireOp",EDGE,"E4.15.0.0"),sQuery(id+"F0.wireOp",EDGE,"E4.15.0.1"),sQuery(id+"F0.wireOp",EDGE,"E4.15.0.2"),sQuery(id+"F0.wireOp",EDGE,"E4.16.0.0"),sQuery(id+"F0.wireOp",EDGE,"E4.16.0.1"),sQuery(id+"F0.wireOp",EDGE,"E4.16.0.2"),sQuery(id+"F0.wireOp",EDGE,"E4.17.0.0"),sQuery(id+"F0.wireOp",EDGE,"E4.17.0.1"),sQuery(id+"F0.wireOp",EDGE,"E4.17.0.2"),sQuery(id+"F0.wireOp",EDGE,"E4.18.0.0"),sQuery(id+"F0.wireOp",EDGE,"E4.18.0.1"),sQuery(id+"F0.wireOp",EDGE,"E4.18.0.2"),sQuery(id+"F0.wireOp",EDGE,"E4.19.0.0"),sQuery(id+"F0.wireOp",EDGE,"E4.19.0.1"),sQuery(id+"F0.wireOp",EDGE,"E4.19.0.2"),sQuery(id+"F0.wireOp",EDGE,"E4.20.0.0"),sQuery(id+"F0.wireOp",EDGE,"E4.20.0.1"),sQuery(id+"F0.wireOp",EDGE,"E4.20.0.2"),sQuery(id+"F0.wireOp",EDGE,"E4.21.0.0"),sQuery(id+"F0.wireOp",EDGE,"E4.21.0.1"),sQuery(id+"F0.wireOp",EDGE,"E4.21.0.2"),sQuery(id+"F0.wireOp",EDGE,"E4.22.0.0"),sQuery(id+"F0.wireOp",EDGE,"E4.22.0.1"),sQuery(id+"F0.wireOp",EDGE,"E4.22.0.2"),sQuery(id+"F0.wireOp",EDGE,"E4.23.0.0"),sQuery(id+"F0.wireOp",EDGE,"E4.23.0.1"),sQuery(id+"F0.wireOp",EDGE,"E4.23.0.2"),sQuery(id+"F0.wireOp",EDGE,"E4.24.0.0"),sQuery(id+"F0.wireOp",EDGE,"E4.24.0.1"),sQuery(id+"F0.wireOp",EDGE,"E4.24.0.2"),sQuery(id+"F0.wireOp",EDGE,"E4.25.0.0"),sQuery(id+"F0.wireOp",EDGE,"E4.25.0.1"),sQuery(id+"F0.wireOp",EDGE,"E4.25.0.2"),sQuery(id+"F0.wireOp",EDGE,"E4.26.0.0"),sQuery(id+"F0.wireOp",EDGE,"E4.26.0.1"),sQuery(id+"F0.wireOp",EDGE,"E4.26.0.2"),sQuery(id+"F0.wireOp",EDGE,"E5.0.27.0"),sQuery(id+"F0.wireOp",EDGE,"E5.3.27.0"),sQuery(id+"F0.wireOp",EDGE,"E5.6.27.0"),sQuery(id+"F0.wireOp",EDGE,"E6.0.28.0"),sQuery(id+"F0.wireOp",EDGE,"E6.3.28.0"),sQuery(id+"F0.wireOp",EDGE,"E6.6.28.0")])],"isStart":true});
            var sketch = newSketch(context, id + "F6", { "sketchPlane" : qUnion([Q0])});
            skEllipse(sketch, "E12", {"center": v(0, 0) * mm, "majorRadius": 40 * mm, "minorRadius": 6.5 * mm, "majorAxis": v(1, 0)});
            skPoint(sketch, "E13", {"position": v(0, 6.5) * mm});
            skPoint(sketch, "E14", {"position": v(40, 0) * mm});
            skPoint(sketch, "E15", {"position": v(0, -6.5) * mm});
            skPoint(sketch, "E16", {"position": v(-40, 0) * mm});
            skSolve(sketch);
        }
        {
            var Q0;
            Q0=makeQuery(id+"F6.imprint","IMPRINT",FACE,{"disambiguationData":[TD([[makeQuery(id+"F6.imprint","IMPRINT",EDGE,{"derivedFrom":sQuery(id+"F6.wireOp",EDGE,"E12")}),1.0]])]});
            extrude(context, id + "F7", {"entities" : qUnion([Q0]), "operationType" : NewBodyOperationType.REMOVE, "oppositeDirection" : true, "depth" : 0.5 * mm, "offsetDistance" : 25 * mm});
        }
        {
            var Q0;
            Q0=makeQuery(id+"F7.boolean.opBoolean","COPY",FACE,{"derivedFrom":makeQuery(id+"F7.opExtrude","CAP_FACE",FACE,{"disambiguationData":[OSD([sQuery(id+"F6.wireOp",EDGE,"E12")])],"isStart":false})});
            fillet(context, id + "F8", {"entities" : qUnion([Q0]), "radius" : 5 * mm, "tangentPropagation" : true, "allowEdgeOverflow" : false});
        }
    });
